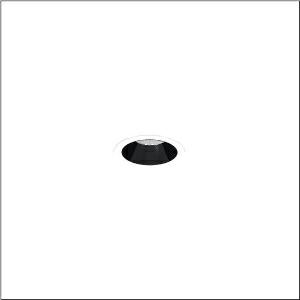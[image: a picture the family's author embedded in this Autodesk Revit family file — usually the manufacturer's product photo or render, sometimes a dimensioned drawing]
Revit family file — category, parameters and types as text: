
# Revit family: lunis_21_s_51db17ma91c
name_source: partatom
category: Lighting Fixtures
units: mm (PartAtom-declared; Revit-internal decimal feet)

## family parameters
Cut with Voids When Loaded = No
Host = Face
Light Source = No
Part Type = Normal
Room Calculation Point = No
Round Connector Dimension = Use Diameter
Shared = No

## types (1)
- --- (1 x LED, 840 lm, 5.9 W, 4000K)
    Apparent Load = 6 VA
    CIE Flux Codes = 95 100 100 100 100
    Color Rendering = 80
    Color Temperature = 4000K
    Default Elevation = 1800 mm
    Description = Lunis 21,  S, downlight, light control with lens, of PMMA, anti glare with reflector, of PC, light emission: direct distribution, LED rated luminous flux: 840lm, light colour: 830/840/865, with terminal, 3-pole, mains connection: 220..240V, AC, 50..60Hz, housing, round, of diecast aluminium, traffic white (RAL 9016), diameter: 84mm, clamping range: 1..40mm, protection rating (complete): IP20, protection rating (on room side): IP54, insulation class (complete): insulation class II (safety insulation), certification: CE, impact resistance: IK03, packaging unit: 1 piece
    Height = 0 mm  [stored 0 ft]
    Lamp = 1 x LED
    Lamp Light Flux = 840 lm
    Lamp Power = 5.9 W
    Lamp count = 1
    Length = 84 mm
    Luminous efficacy = 142 lm/W
    Manufacturer = Siteco
    ModVariant = No
    Model = 51DB17MA91C
    Mounting Place = Ceiling
    Mounting Type = Recessed
    Number of Poles = 1
    OnlyDefault = Yes
    Power Factor = 1
    Product Name = Lunis 21 S
    Product group = downlight
    ProductGroupID = 400
    Protection Class = Protection class II
    Protection Degree = IP 20
    RLX_Detail_Level = 1
    RLX_Emergency_Light_Flux = 0 lm
    RLX_Emergency_Type = 0
    RLX_Emergency_Type_DB = No
    RlxData = <blob elided: 8301 chars, md5=51a04f5e>
    Socket = socket
    Standby Power = 0 W
    System Light Flux = 840 lm
    System Power = 6 W
    Type Comments = factory setting: colour temperature 4000K
    Type Image = l_1290844.jpg
    URL = http://relux.com
    VarID = @adj_017537
    Voltage = 0 V
    Weight = 0.00 kg
    Width = 0 mm  [stored 0 ft]

note: [stored X ft] marks values corroborated as IEEE doubles in the binary element streams (Revit-internal decimal feet)

## geometry (parser evidence)
native form markers: Sweep x9
no freeform markers — native parametric forms only
